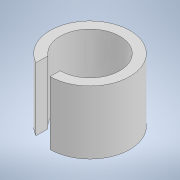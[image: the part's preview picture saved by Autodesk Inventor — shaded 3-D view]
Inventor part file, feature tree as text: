
AUTODESK INVENTOR PART (.ipt)
format: ipt  version: 2022 (Build 260153000, 153)  size: 103,936 bytes
history: native  units: in
note: dims shown in document units (in); Inventor stores cm internally (conversion verified against a paired STEP export)
features: extrude x1, sketch x1
ambient origin geometry x8: Origin, YZ Plane, XZ Plane, XY Plane, X Axis, Y Axis, Z Axis, Center Point
bodies: Solid1 (feature_tree)
feature tree (2):
  extrude  "Extrusion1"  Depth=0.075in
  sketch  "Sketch1"  dims[d0=0.2362in d1=0.315in d2=0.25in d3=0.0in d4=0.075in d5=0.075in]
